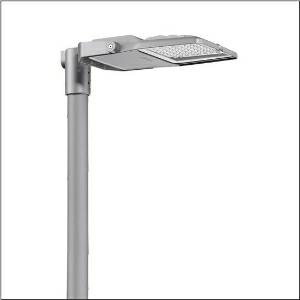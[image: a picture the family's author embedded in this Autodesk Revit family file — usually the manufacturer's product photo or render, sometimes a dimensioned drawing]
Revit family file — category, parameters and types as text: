
# Revit family: floodlight_fl_21_iq_mini___pl43_5xa7771d2a3a_a639
name_source: partatom
category: Lighting Fixtures
units: mm (PartAtom-declared; Revit-internal decimal feet)

## family parameters
Cut with Voids When Loaded = No
Host = Face
Light Source = No
Part Type = Normal
Room Calculation Point = No
Round Connector Dimension = Use Diameter
Shared = No

## types (1)
- --- (1 x LED, 18290 lm, 143 W, 3000K)
    Apparent Load = 143 VA
    CIE Flux Codes = 27 78 99 100 100
    Color Rendering = 70
    Color Temperature = 3000K
    Default Elevation = 1800 mm
    Description = Floodlight FL 21 iQ mini, floodlight, primary light control with lens, of PMMA, primary optical cover: protective disc, of toughened safety glass, transparent, light distribution: PL43, light emission: direct distribution, installation type: surface-mounted, lamps: LED, High Power LED, rated values: 18.290lm | 143W | 127,9lm/W (begin service life); end service life: 18.290lm | 151,6W; at 50% lumin. flux: 9.145lm | 60,6W | 150,9lm/W, colour temperature: 3000K, colour rendering: CRI > 70, light colour: 730, light setting 1 begin service life: 100% | 18.290lm | 143W | 127,9lm/W | 3.000K, light setting 1 end service life: 151,6W, further light settings possible, control: Auto-Match, Temp-Guard, Lumen-Switch, Night-Set, Smart-Wire, Light-Fading, Desk-Remote (wireless, voltage-free reading and setting of iQ features in the workshop via application-optimized NFC function/RFID function), optimised constant luminous flux control (CLO 2.0), pre-setting: linear dimming characteristic, with terminal, 6-pole, mains connection: 220..240V, AC, 50/60Hz, luminaire housing, of diecast aluminium, powder-coated, SITECO metallic grey (DB 702S), corrosivity category C5 mid according to DIN EN ISO 12944suitable for swimming poolschlorine-resistant, sealing non-destructively replaceable, please order mast flange separately, mast bracket, of steel, galvanised, powder-coated, SITECO metallic grey (DB 702S), protection rating (complete): IP66, insulation class (complete): insulation class II (safety insulation), certification: CE, ENEC, VDE, protection symbol: D, impact resistance: IK08, permissible operating ambient temperature: -40..+40°C, permissible operating ambient temperature for outdoor applications: -40..+50°C, standard: DIN EN 12944, LABS conformity tested according to VDMA 24364:2018-05, packaging unit: 1 piece

Light Distribution: PL43
    Height = 70 mm
    Lamp = 1 x LED
    Lamp Light Flux = 18290 lm
    Lamp Power = 143 W
    Lamp count = 1
    Length = 485 mm
    Luminous efficacy = 128 lm/W
    Manufacturer = Siteco
    ModVariant = No
    Model = 5XA7771D2A3A
    Number of Poles = 1
    OnlyDefault = Yes
    Power Factor = 1
    Product Name = Floodlight FL 21 iQ mini | PL43
    Product group = floodlight | pylon annexe
    ProductGroupID = 6201
    Protection Class = Protection class II
    Protection Degree = IP 66
    RLX_Detail_Level = 1
    RLX_Emergency_Light_Flux = 0 lm
    RLX_Emergency_Type = 0
    RLX_Emergency_Type_DB = No
    RlxData = <blob elided: 101761 chars, md5=f4f2249f>
    Socket = socket
    Standby Power = 0 W
    System Light Flux = 18290 lm
    System Power = 143 W
    Type Comments = factory setting: luminous flux: 100 % | dim-lin: 254 | 730 mA
    Type Image = l_1007125.jpg
    URL = http://relux.com
    VarID = @adj_161327
    Voltage = 0 V
    Weight = 0.00 kg
    Width = 337 mm

## geometry (parser evidence)
native form markers: Blend x4, Sweep x13
no freeform markers — native parametric forms only
